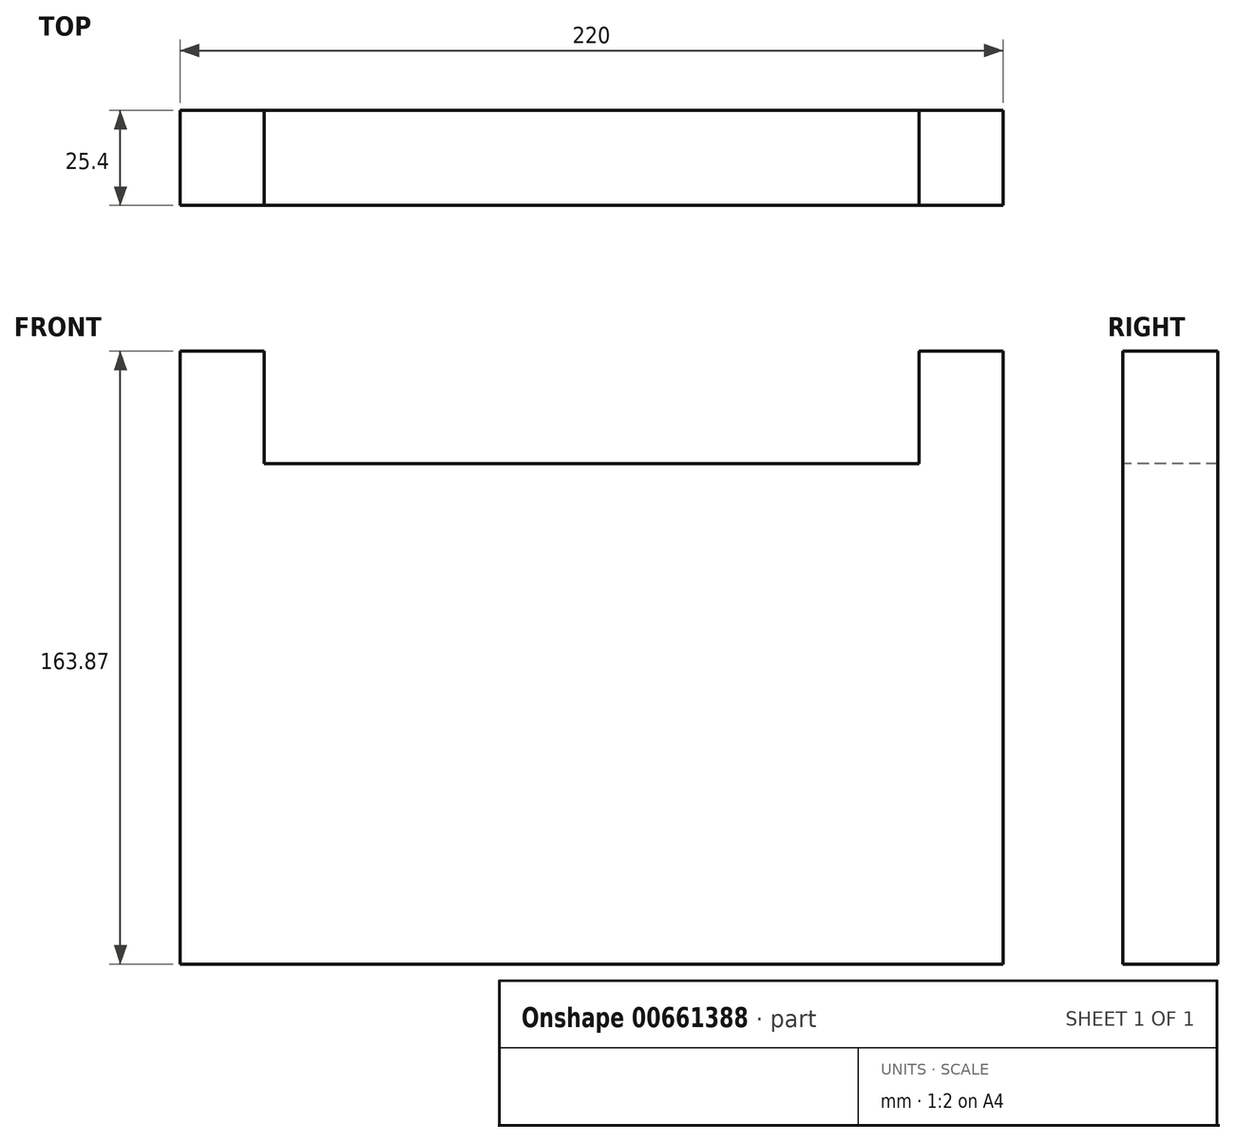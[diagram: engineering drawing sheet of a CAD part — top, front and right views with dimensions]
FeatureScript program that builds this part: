
annotation { "Feature Type Name" : "Feature", "Feature Type Description" : "" }
export const myFeature = defineFeature(function(context is Context, id is Id, definition is map)
    precondition{}
    {
        {
            var Q0;
            Q0=qCreatedBy(makeId("Front.planeOp"),FACE);
            var sketch = newSketch(context, id + "F0", { "sketchPlane" : qUnion([Q0])});
            skLineSegment(sketch, "E0.bottom", {"start": v(-108.69, 80.18) * mm, "end": v(111.31, 80.18) * mm});
            skLineSegment(sketch, "E0.top", {"start": v(-108.69, -83.69) * mm, "end": v(111.31, -83.69) * mm});
            skLineSegment(sketch, "E0.left", {"start": v(-108.69, 80.18) * mm, "end": v(-108.69, -83.69) * mm});
            skLineSegment(sketch, "E0.right", {"start": v(111.31, 80.18) * mm, "end": v(111.31, -83.69) * mm});
            skSolve(sketch);
        }
        {
            var Q0;
            Q0=makeQuery(id+"F0.imprint","IMPRINT",FACE,{"disambiguationData":[TD([[makeQuery(id+"F0.imprint","IMPRINT",EDGE,{"derivedFrom":sQuery(id+"F0.wireOp",EDGE,"E0.bottom")}),-1.0]])]});
            extrude(context, id + "F1", {"entities" : qUnion([Q0]), "depth" : 25.4 * mm, "offsetDistance" : 25.4 * mm});
        }
        {
            var Q0;
            Q0=makeQuery(id+"F1.opExtrude","CAP_FACE",FACE,{"disambiguationData":[OSD([sQuery(id+"F0.wireOp",EDGE,"E0.bottom"),sQuery(id+"F0.wireOp",EDGE,"E0.top"),sQuery(id+"F0.wireOp",EDGE,"E0.left"),sQuery(id+"F0.wireOp",EDGE,"E0.right")])],"isStart":false});
            var sketch = newSketch(context, id + "F2", { "sketchPlane" : qUnion([Q0])});
            skLineSegment(sketch, "E1.bottom", {"start": v(-86.29, 80.18) * mm, "end": v(88.91, 80.18) * mm});
            skLineSegment(sketch, "E1.top", {"start": v(-86.29, 50.18) * mm, "end": v(88.91, 50.18) * mm});
            skLineSegment(sketch, "E1.left", {"start": v(-86.29, 80.18) * mm, "end": v(-86.29, 50.18) * mm});
            skLineSegment(sketch, "E1.right", {"start": v(88.91, 80.18) * mm, "end": v(88.91, 50.18) * mm});
            skLineSegment(sketch, "E2", {"start": v(-108.69, 80.18) * mm, "end": v(-86.29, 80.18) * mm});
            skLineSegment(sketch, "E3", {"start": v(88.91, 80.18) * mm, "end": v(111.31, 80.18) * mm});
            skLineSegment(sketch, "E4", {"start": v(-86.29, 50.18) * mm, "end": v(-108.69, 50.18) * mm});
            skLineSegment(sketch, "E5", {"start": v(88.91, 50.18) * mm, "end": v(111.31, 50.18) * mm});
            skSolve(sketch);
        }
        {
            var Q0;
            Q0=makeQuery(id+"F2.imprint","IMPRINT",FACE,{"disambiguationData":[TD([[makeQuery(id+"F2.imprint","IMPRINT",EDGE,{"derivedFrom":sQuery(id+"F2.wireOp",EDGE,"nbMupDO8-Tt4J-jYjU-eP9p-dOQ1Q0qhNvrF")}),1.0]])]});
            var Q1;
            Q1=makeQuery(id+"F2.imprint","IMPRINT",FACE,{"disambiguationData":[TD([[makeQuery(id+"F2.imprint","IMPRINT",EDGE,{"derivedFrom":sQuery(id+"F2.wireOp",EDGE,"E1.bottom")}),-1.0]])]});
            extrude(context, id + "F3", {"entities" : qUnion([Q0, Q1]), "operationType" : NewBodyOperationType.REMOVE, "oppositeDirection" : true, "depth" : 57.15 * mm, "offsetDistance" : 25.4 * mm});
        }
    });
